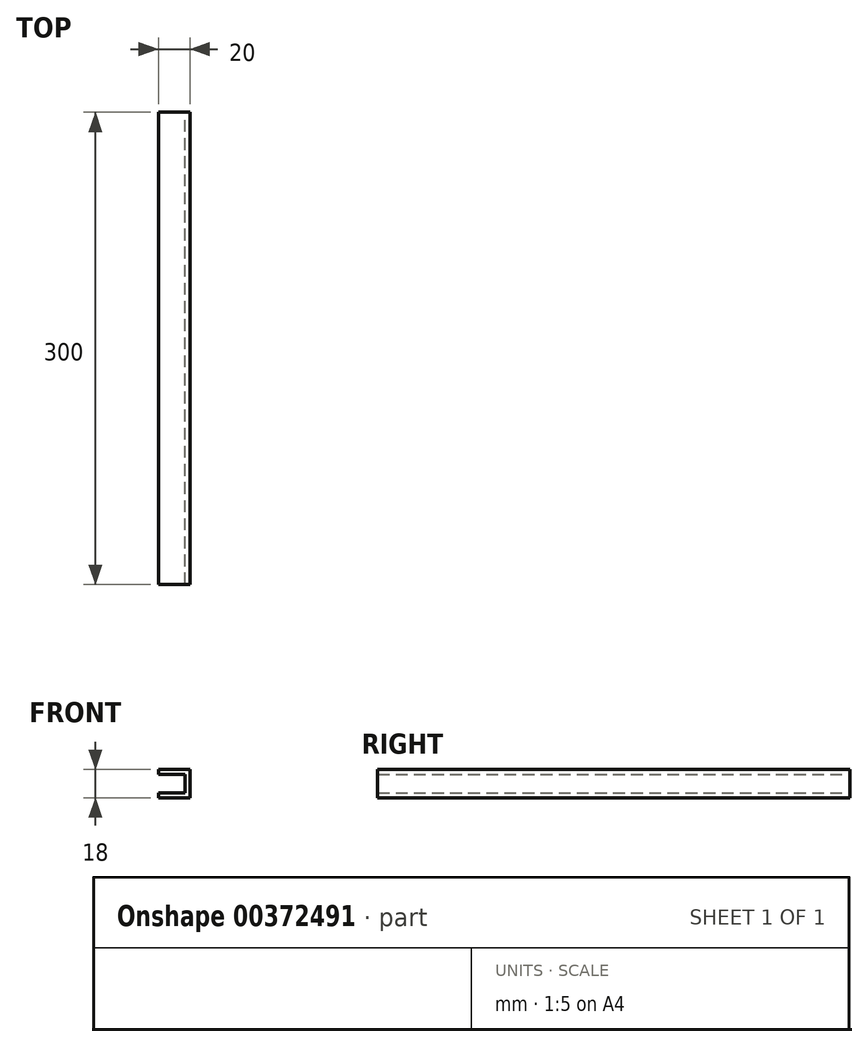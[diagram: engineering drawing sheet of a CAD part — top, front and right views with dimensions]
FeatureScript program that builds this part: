
annotation { "Feature Type Name" : "Feature", "Feature Type Description" : "" }
export const myFeature = defineFeature(function(context is Context, id is Id, definition is map)
    precondition{}
    {
        {
            var Q0;
            Q0=qCreatedBy(makeId("Top.planeOp"),FACE);
            var sketch = newSketch(context, id + "F0", { "sketchPlane" : qUnion([Q0])});
            skLineSegment(sketch, "E0.bottom", {"start": v(150, 150) * mm, "end": v(-150, 150) * mm});
            skLineSegment(sketch, "E0.top", {"start": v(150, -150) * mm, "end": v(-150, -150) * mm});
            skLineSegment(sketch, "E0.left", {"start": v(150, 150) * mm, "end": v(150, -150) * mm});
            skLineSegment(sketch, "E0.right", {"start": v(-150, 150) * mm, "end": v(-150, -150) * mm});
            skPoint(sketch, "E0.middle", {"position": v(0, 0) * mm});
            skSolve(sketch);
        }
        {
            var Q0;
            Q0=qCreatedBy(makeId("Front.planeOp"),FACE);
            var sketch = newSketch(context, id + "F1", { "sketchPlane" : qUnion([Q0])});
            skLineSegment(sketch, "E1", {"start": v(-150, 0) * mm, "end": v(-170, 0) * mm});
            skLineSegment(sketch, "E2", {"start": v(-170, 0) * mm, "end": v(-170, 3) * mm});
            skLineSegment(sketch, "E3", {"start": v(-170, 3) * mm, "end": v(-153, 3) * mm});
            skLineSegment(sketch, "E4", {"start": v(-153, 3) * mm, "end": v(-153, 15) * mm});
            skLineSegment(sketch, "E5", {"start": v(-153, 15) * mm, "end": v(-170, 15) * mm});
            skLineSegment(sketch, "E6", {"start": v(-170, 15) * mm, "end": v(-170, 18) * mm});
            skLineSegment(sketch, "E7", {"start": v(-170, 18) * mm, "end": v(-150, 18) * mm});
            skLineSegment(sketch, "E8", {"start": v(-150, 18) * mm, "end": v(-150, 0) * mm});
            skSolve(sketch);
        }
        {
            var Q0;
            Q0 = qSketchRegion(id + "F1", true);
            var Q1;
            Q1=sQuery(id+"F0.wireOp",VERTEX,"E0.right.end");
            var Q2;
            Q2=sQuery(id+"F0.wireOp",VERTEX,"E0.right.start");
            extrude(context, id + "F2", {"entities" : qUnion([Q0]), "endBound" : BoundingType.UP_TO_VERTEX, "endBoundEntityVertex" : qUnion([Q1]), "depth" : 25 * mm, "hasSecondDirection" : true, "secondDirectionBound" : SecondDirectionBoundingType.UP_TO_VERTEX, "secondDirectionOppositeDirection" : true, "secondDirectionBoundEntityVertex" : qUnion([Q2]), "secondDirectionDepth" : 25 * mm});
        }
    });
